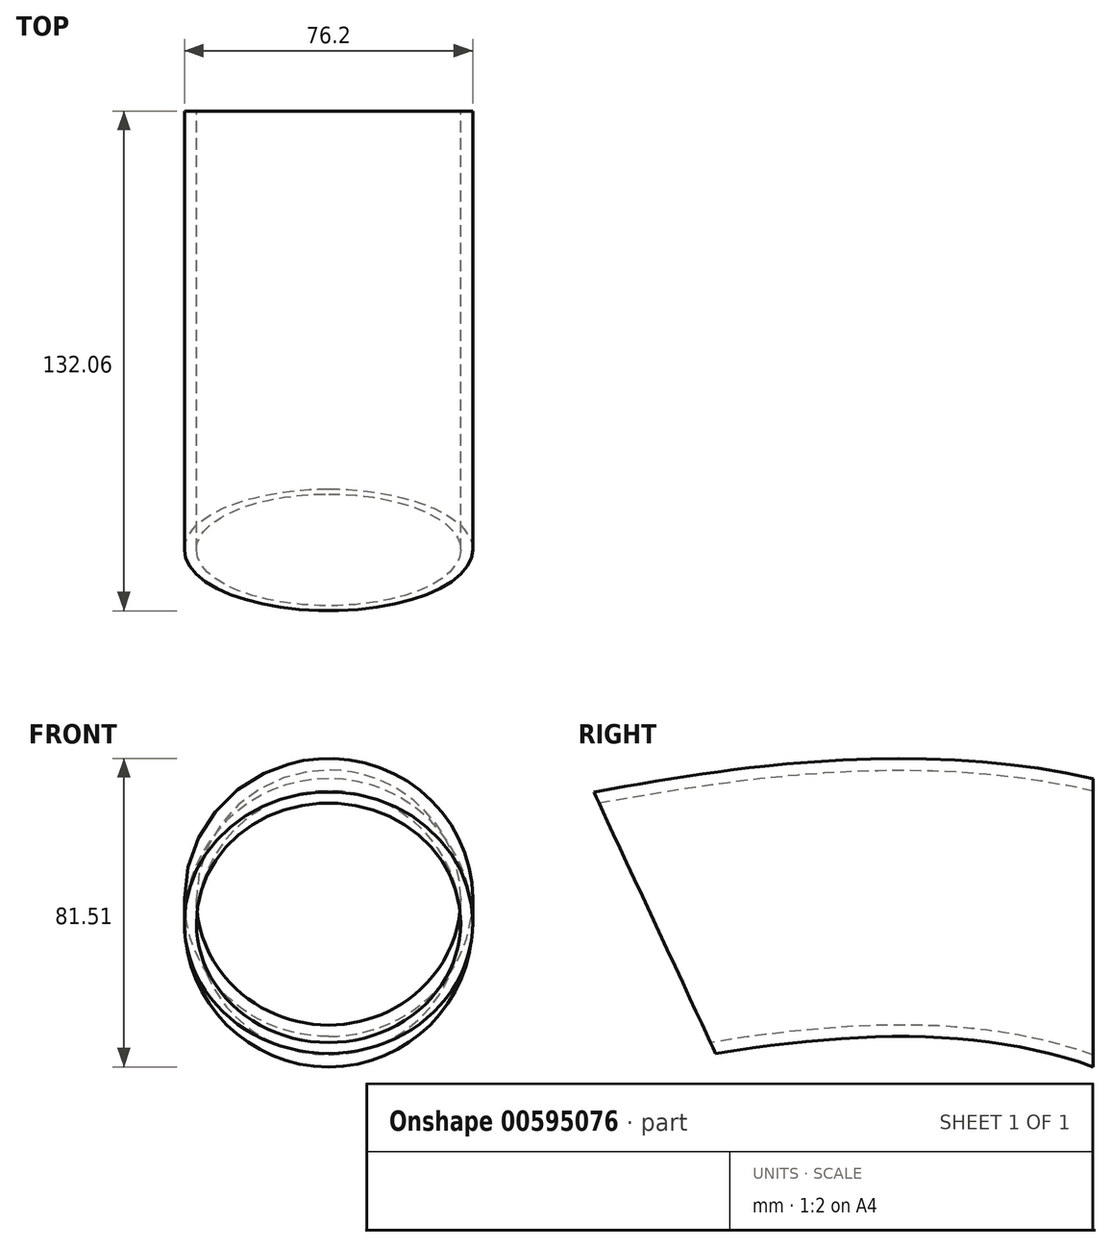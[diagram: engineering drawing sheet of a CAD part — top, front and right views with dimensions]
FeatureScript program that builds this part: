
annotation { "Feature Type Name" : "Feature", "Feature Type Description" : "" }
export const myFeature = defineFeature(function(context is Context, id is Id, definition is map)
    precondition{}
    {
        {
            var Q0;
            Q0=qCreatedBy(makeId("Front.planeOp"),FACE);
            var sketch = newSketch(context, id + "F0", { "sketchPlane" : qUnion([Q0])});
            skCircle(sketch, "E0", {"center": v(0, 0) * mm, "radius": 38.1 * mm});
            skCircle(sketch, "E1", {"center": v(0, 0) * mm, "radius": 34.93 * mm});
            skSolve(sketch);
        }
        {
            var Q0;
            Q0=qCreatedBy(makeId("Right.planeOp"),FACE);
            var sketch = newSketch(context, id + "F1", { "sketchPlane" : qUnion([Q0])});
            skFitSpline(sketch, "E2", {"points": [v(0, 0) * mm, v(-115.95, 0) * mm], "startDerivative": vector(-113.49, 31.03) * mm, "endDerivative": vector(-117.7, -20.14) * mm});
            skSolve(sketch);
        }
        {
            var Q0;
            Q0=makeQuery(id+"F0.imprint","IMPRINT",FACE,{"disambiguationData":[TD([[makeQuery(id+"F0.imprint","IMPRINT",EDGE,{"derivedFrom":sQuery(id+"F0.wireOp",EDGE,"E0")}),1.0]])]});
            var Q1;
            Q1=sQuery(id+"F1.wireOp",EDGE,"E2");
            sweep(context, id + "F2", {"profiles" : qUnion([Q0]), "path" : qUnion([Q1])});
        }
    });
